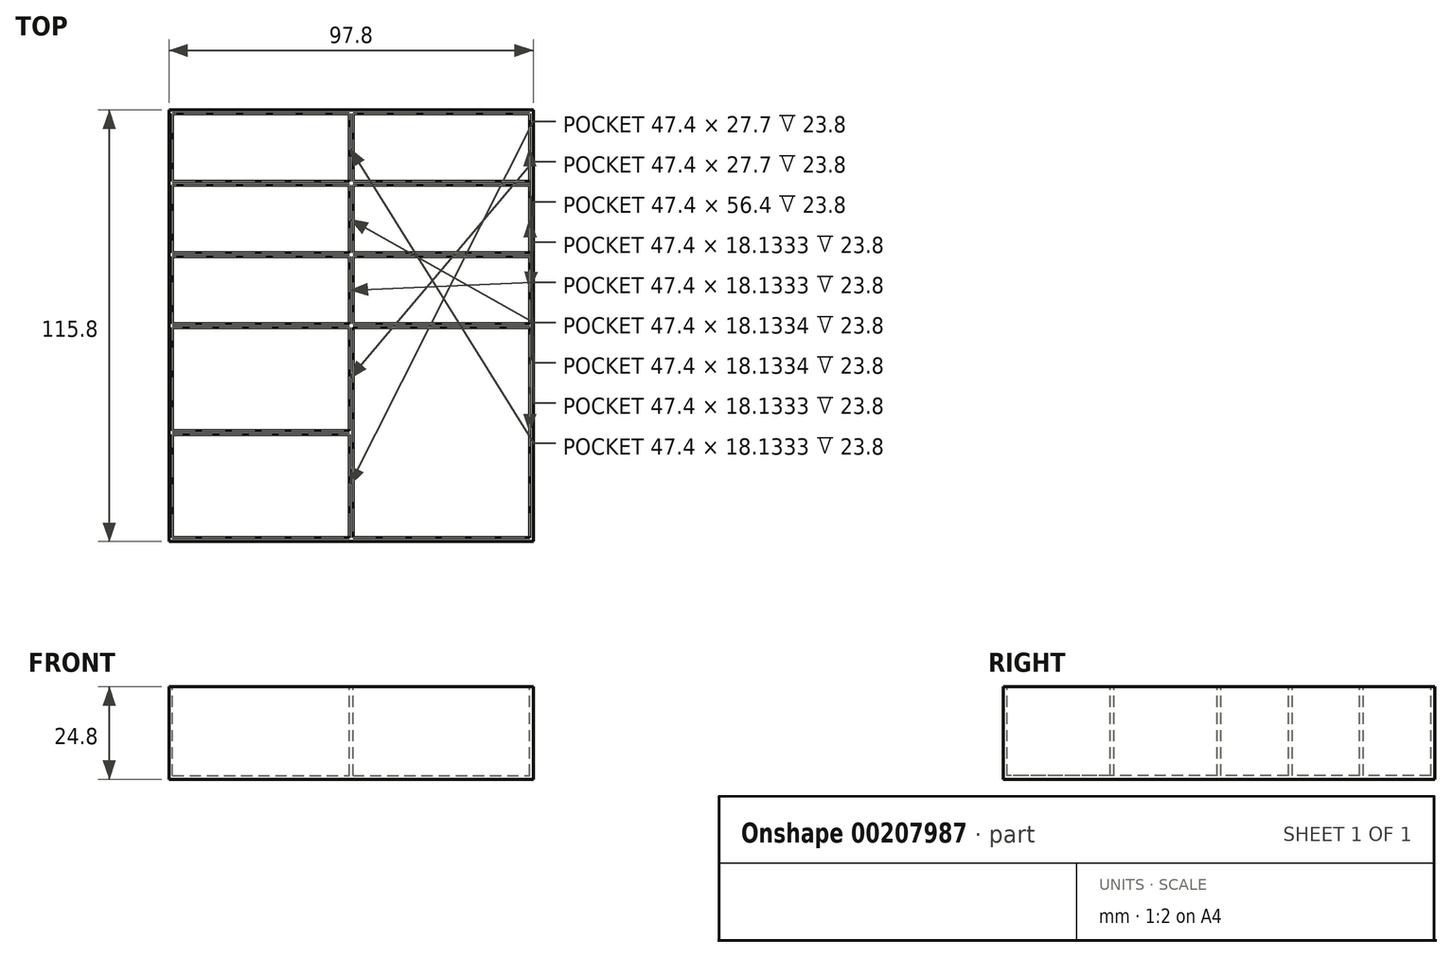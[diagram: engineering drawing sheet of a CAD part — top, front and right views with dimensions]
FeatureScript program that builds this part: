
annotation { "Feature Type Name" : "Feature", "Feature Type Description" : "" }
export const myFeature = defineFeature(function(context is Context, id is Id, definition is map)
    precondition{}
    {
        {
            var Q0;
            Q0=qCreatedBy(makeId("Top.planeOp"),FACE);
            var sketch = newSketch(context, id + "F0", { "sketchPlane" : qUnion([Q0])});
            skLineSegment(sketch, "E0.bottom", {"start": v(-51.66, 56.4) * mm, "end": v(46.14, 56.4) * mm});
            skLineSegment(sketch, "E0.top", {"start": v(-51.66, -59.4) * mm, "end": v(46.14, -59.4) * mm});
            skLineSegment(sketch, "E0.left", {"start": v(-51.66, 56.4) * mm, "end": v(-51.66, -59.4) * mm});
            skLineSegment(sketch, "E0.right", {"start": v(46.14, 56.4) * mm, "end": v(46.14, -59.4) * mm});
            skSolve(sketch);
        }
        {
            var Q0;
            Q0 = qSketchRegion(id + "F0", true);
            var Q1;
            Q1=makeQuery(id+"F0.imprint","IMPRINT",FACE,{"disambiguationData":[TD([[makeQuery(id+"F0.imprint","IMPRINT",EDGE,{"derivedFrom":sQuery(id+"F0.wireOp",EDGE,"E0.bottom")}),-1.0]])]});
            extrude(context, id + "F1", {"entities" : qUnion([Q0, Q1]), "depth" : 24.8 * mm});
        }
        {
            var Q0;
            Q0=makeQuery(id+"F1.opExtrude","CAP_FACE",FACE,{"disambiguationData":[OSD([sQuery(id+"F0.wireOp",EDGE,"E0.bottom"),sQuery(id+"F0.wireOp",EDGE,"E0.top"),sQuery(id+"F0.wireOp",EDGE,"E0.left"),sQuery(id+"F0.wireOp",EDGE,"E0.right")])],"isStart":false});
            var sketch = newSketch(context, id + "F2", { "sketchPlane" : qUnion([Q0])});
            skLineSegment(sketch, "E1", {"start": v(-51.66, -1.5) * mm, "end": v(46.14, -1.5) * mm, "construction": true});
            skLineSegment(sketch, "E2", {"start": v(-2.76, -59.4) * mm, "end": v(-2.76, 56.4) * mm, "construction": true});
            skLineSegment(sketch, "E3.bottom", {"start": v(-50.66, -30.7) * mm, "end": v(-3.26, -30.7) * mm});
            skLineSegment(sketch, "E3.top", {"start": v(-50.66, -58.4) * mm, "end": v(-3.26, -58.4) * mm});
            skLineSegment(sketch, "E3.left", {"start": v(-50.66, -30.7) * mm, "end": v(-50.66, -58.4) * mm});
            skLineSegment(sketch, "E3.right", {"start": v(-3.26, -30.7) * mm, "end": v(-3.26, -58.4) * mm});
            skLineSegment(sketch, "E4.bottom", {"start": v(-2.26, -2) * mm, "end": v(45.14, -2) * mm});
            skLineSegment(sketch, "E4.top", {"start": v(-2.26, -58.4) * mm, "end": v(45.14, -58.4) * mm});
            skLineSegment(sketch, "E4.left", {"start": v(-2.26, -2) * mm, "end": v(-2.26, -58.4) * mm});
            skLineSegment(sketch, "E4.right", {"start": v(45.14, -2) * mm, "end": v(45.14, -58.4) * mm});
            skLineSegment(sketch, "E5.bottom", {"start": v(-50.66, 55.4) * mm, "end": v(-3.26, 55.4) * mm});
            skLineSegment(sketch, "E5.top", {"start": v(-50.66, 37.28) * mm, "end": v(-3.26, 37.28) * mm});
            skLineSegment(sketch, "E5.left", {"start": v(-50.66, 55.4) * mm, "end": v(-50.66, 37.28) * mm});
            skLineSegment(sketch, "E5.right", {"start": v(-3.26, 55.4) * mm, "end": v(-3.26, 37.28) * mm});
            skLineSegment(sketch, "E6.bottom", {"start": v(-50.66, 36.28) * mm, "end": v(-3.26, 36.28) * mm});
            skLineSegment(sketch, "E6.top", {"start": v(-50.66, 18.14) * mm, "end": v(-3.26, 18.14) * mm});
            skLineSegment(sketch, "E6.left", {"start": v(-50.66, 36.28) * mm, "end": v(-50.66, 18.14) * mm});
            skLineSegment(sketch, "E6.right", {"start": v(-3.26, 36.28) * mm, "end": v(-3.26, 18.14) * mm});
            skLineSegment(sketch, "E7.bottom", {"start": v(-2.26, 55.4) * mm, "end": v(45.14, 55.4) * mm});
            skLineSegment(sketch, "E7.top", {"start": v(-2.26, 37.28) * mm, "end": v(45.14, 37.28) * mm});
            skLineSegment(sketch, "E7.left", {"start": v(-2.26, 55.4) * mm, "end": v(-2.26, 37.28) * mm});
            skLineSegment(sketch, "E7.right", {"start": v(45.14, 55.4) * mm, "end": v(45.14, 37.28) * mm});
            skLineSegment(sketch, "E8.bottom", {"start": v(-2.26, 36.28) * mm, "end": v(45.14, 36.28) * mm});
            skLineSegment(sketch, "E8.top", {"start": v(-2.26, 18.14) * mm, "end": v(45.14, 18.14) * mm});
            skLineSegment(sketch, "E8.left", {"start": v(-2.26, 36.28) * mm, "end": v(-2.26, 18.14) * mm});
            skLineSegment(sketch, "E8.right", {"start": v(45.14, 36.28) * mm, "end": v(45.14, 18.14) * mm});
            skLineSegment(sketch, "E9.bottom", {"start": v(-2.26, 17.14) * mm, "end": v(45.14, 17.14) * mm});
            skLineSegment(sketch, "E9.top", {"start": v(-2.26, -1) * mm, "end": v(45.14, -1) * mm});
            skLineSegment(sketch, "E9.left", {"start": v(-2.26, 17.14) * mm, "end": v(-2.26, -1) * mm});
            skLineSegment(sketch, "E9.right", {"start": v(45.14, 17.14) * mm, "end": v(45.14, -1) * mm});
            skLineSegment(sketch, "E10.bottom", {"start": v(-50.66, 17.14) * mm, "end": v(-3.26, 17.14) * mm});
            skLineSegment(sketch, "E10.top", {"start": v(-50.66, -1) * mm, "end": v(-3.26, -1) * mm});
            skLineSegment(sketch, "E10.left", {"start": v(-50.66, 17.14) * mm, "end": v(-50.66, -1) * mm});
            skLineSegment(sketch, "E10.right", {"start": v(-3.26, 17.14) * mm, "end": v(-3.26, -1) * mm});
            skLineSegment(sketch, "E11.bottom", {"start": v(-50.66, -2) * mm, "end": v(-3.26, -2) * mm});
            skLineSegment(sketch, "E11.top", {"start": v(-50.66, -29.7) * mm, "end": v(-3.26, -29.7) * mm});
            skLineSegment(sketch, "E11.left", {"start": v(-50.66, -2) * mm, "end": v(-50.66, -29.7) * mm});
            skLineSegment(sketch, "E11.right", {"start": v(-3.26, -2) * mm, "end": v(-3.26, -29.7) * mm});
            skSolve(sketch);
        }
        {
            var Q0;
            Q0=makeQuery(id+"F2.imprint","IMPRINT",FACE,{"disambiguationData":[TD([[makeQuery(id+"F2.imprint","IMPRINT",EDGE,{"derivedFrom":sQuery(id+"F2.wireOp",EDGE,"E3.bottom")}),-1.0]])]});
            var Q1;
            Q1=makeQuery(id+"F2.imprint","IMPRINT",FACE,{"disambiguationData":[TD([[makeQuery(id+"F2.imprint","IMPRINT",EDGE,{"derivedFrom":sQuery(id+"F2.wireOp",EDGE,"E11.bottom")}),-1.0]])]});
            var Q2;
            Q2=makeQuery(id+"F2.imprint","IMPRINT",FACE,{"disambiguationData":[TD([[makeQuery(id+"F2.imprint","IMPRINT",EDGE,{"derivedFrom":sQuery(id+"F2.wireOp",EDGE,"E4.bottom")}),-1.0]])]});
            var Q3;
            Q3=makeQuery(id+"F2.imprint","IMPRINT",FACE,{"disambiguationData":[TD([[makeQuery(id+"F2.imprint","IMPRINT",EDGE,{"derivedFrom":sQuery(id+"F2.wireOp",EDGE,"E9.bottom")}),-1.0]])]});
            var Q4;
            Q4=makeQuery(id+"F2.imprint","IMPRINT",FACE,{"disambiguationData":[TD([[makeQuery(id+"F2.imprint","IMPRINT",EDGE,{"derivedFrom":sQuery(id+"F2.wireOp",EDGE,"E10.bottom")}),-1.0]])]});
            var Q5;
            Q5=makeQuery(id+"F2.imprint","IMPRINT",FACE,{"disambiguationData":[TD([[makeQuery(id+"F2.imprint","IMPRINT",EDGE,{"derivedFrom":sQuery(id+"F2.wireOp",EDGE,"E6.bottom")}),-1.0]])]});
            var Q6;
            Q6=makeQuery(id+"F2.imprint","IMPRINT",FACE,{"disambiguationData":[TD([[makeQuery(id+"F2.imprint","IMPRINT",EDGE,{"derivedFrom":sQuery(id+"F2.wireOp",EDGE,"E8.bottom")}),-1.0]])]});
            var Q7;
            Q7=makeQuery(id+"F2.imprint","IMPRINT",FACE,{"disambiguationData":[TD([[makeQuery(id+"F2.imprint","IMPRINT",EDGE,{"derivedFrom":sQuery(id+"F2.wireOp",EDGE,"E7.bottom")}),-1.0]])]});
            var Q8;
            Q8=makeQuery(id+"F2.imprint","IMPRINT",FACE,{"disambiguationData":[TD([[makeQuery(id+"F2.imprint","IMPRINT",EDGE,{"derivedFrom":sQuery(id+"F2.wireOp",EDGE,"E5.bottom")}),-1.0]])]});
            extrude(context, id + "F3", {"entities" : qUnion([Q0, Q1, Q2, Q3, Q4, Q5, Q6, Q7, Q8]), "operationType" : NewBodyOperationType.REMOVE, "oppositeDirection" : true, "depth" : 23.8 * mm});
        }
    });
